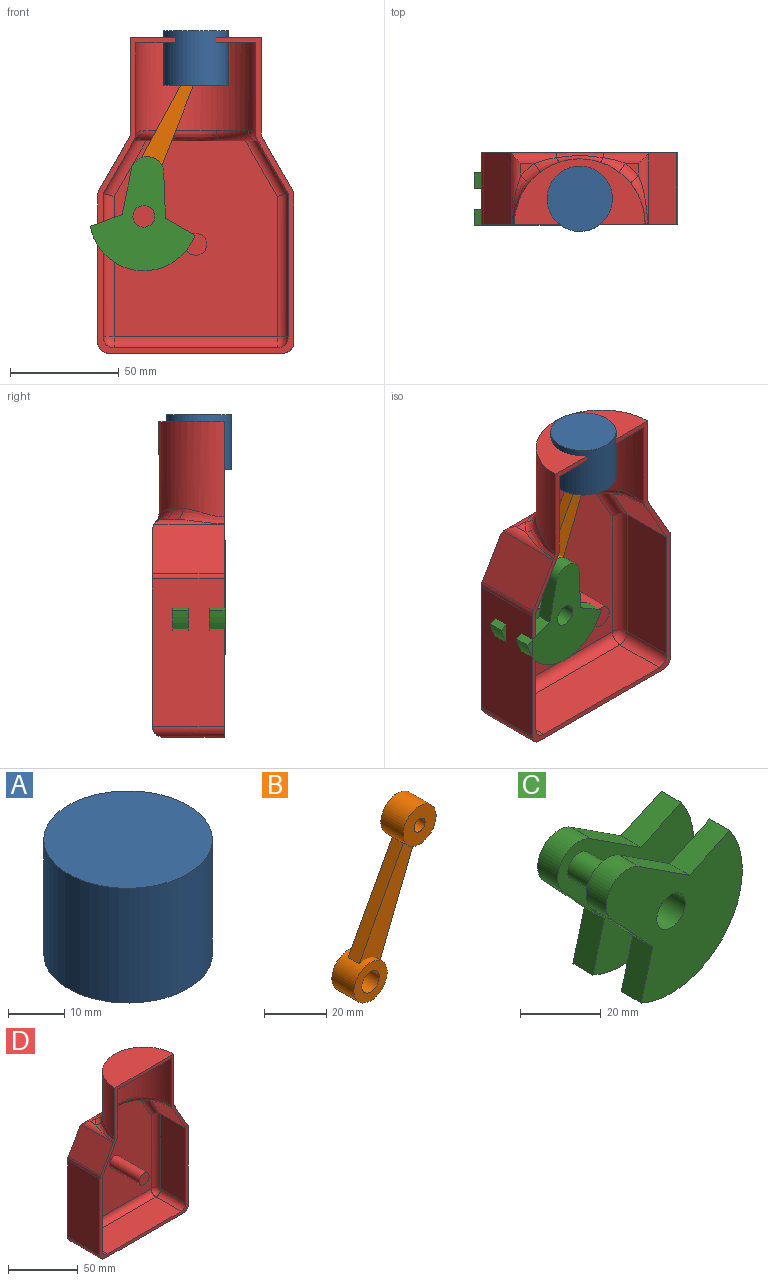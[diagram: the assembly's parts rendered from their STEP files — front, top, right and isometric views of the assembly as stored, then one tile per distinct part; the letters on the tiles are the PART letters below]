
ASSEMBLY  parts=4 mates=3
PART A: 17 faces, bbox 30x30x25 mm
  f0: cylinder r=5mm len=10mm, axis (0,1,0), area 101.5mm2, adj f1,f7,f8,f11
  f1: cylinder r=12mm len=24mm, axis (0,0,1), area 1330.9mm2, adj f0,f2,f3,f6,f7,f8,f9
  f2: plane 21.82x7mm, normal (0,0,-1), area 109.8mm2, adj f1,f7
  f3: plane 30x30mm, normal (0,0,-1), area 254.5mm2, adj f1,f4
  f4: cylinder r=15mm len=30mm, axis (0,0,1), area 2356.2mm2, adj f3,f5
  f5: plane 30x30mm, normal (0,0,1), area 706.9mm2, adj f4
  f6: plane 21.82x7mm, normal (0,0,-1), area 109.8mm2, adj f1,f8
  f7: plane 21.82x12mm, normal (-1,0,0), area 181.8mm2, adj f0,f1,f2,f9,f10,f11,f12
  f8: plane 21.82x12mm, normal (1,0,0), area 181.8mm2, adj f0,f1,f6,f9,f10,f11,f12
  f9: cylinder r=5mm len=10mm, axis (0,1,0), area 101.5mm2, adj f1,f7,f8,f12
  f10: plane 10x10mm, normal (0,0,-1), area 100mm2, adj f7,f8,f11,f12
  f11: plane 13x10mm, normal (0,-1,0), area 99.6mm2, adj f0,f7,f8,f10,f15
  f12: plane 13x10mm, normal (0,1,0), area 99.6mm2, adj f7,f8,f9,f10,f14
  f13: cylinder r=12mm len=5mm, axis (0,0,1), area 19.7mm2, adj f14
  f14: cylinder r=2.5mm len=7mm, axis (0,1,0), area 107.9mm2, adj f12,f13
  f15: cylinder r=2.5mm len=7mm, axis (0,1,0), area 107.9mm2, adj f11,f16
  f16: cylinder r=12mm len=5mm, axis (0,0,1), area 19.7mm2, adj f15
PART B: 12 faces, bbox 37.2x10x65.3 mm
  f0: cylinder r=4mm len=10mm, axis (0,1,0), area 251.3mm2, adj f2,f3
  f1: cylinder r=7.5mm len=15mm, axis (0,1,0), area 416.5mm2, adj f2,f3,f8,f9,f10,f11
  f2: plane 15x15mm, normal (0,-1,0), area 126.4mm2, adj f0,f1
  f3: plane 15x15mm, normal (0,1,0), area 126.4mm2, adj f0,f1
  f4: cylinder r=2.5mm len=10mm, axis (0,1,0), area 157.1mm2, adj f6,f7
  f5: cylinder r=7.5mm len=15mm, axis (0,1,0), area 445.8mm2, adj f6,f7,f8,f9,f10,f11
  f6: plane 15x15mm, normal (0,-1,0), area 157.1mm2, adj f4,f5
  f7: plane 15x15mm, normal (0,1,0), area 157.1mm2, adj f4,f5
  f8: plane 39.37x15.55mm, normal (0.93,0,-0.37), area 211.6mm2, adj f1,f5,f10,f11
  f9: plane 37.48x20.18mm, normal (-0.88,0,0.47), area 212.8mm2, adj f1,f5,f10,f11
  f10: plane 41.03x24.9mm, normal (0,-1,0), area 302.2mm2, adj f1,f5,f8,f9
  f11: plane 41.03x24.9mm, normal (0,1,0), area 302.2mm2, adj f1,f5,f8,f9
PART C: 19 faces, bbox 47.8x24x45.4 mm
  f0: plane 14.12x7mm, normal (-0.42,0,0.91), area 109mm2, adj f1,f6,f7,f10
  f1: plane 17.66x11.48mm, normal (0.55,0,0.84), area 147.5mm2, adj f0,f2,f7,f10
  f2: cylinder r=7.5mm len=12.62mm, axis (0,1,0), area 152.2mm2, adj f1,f3,f7,f10
  f3: plane 15.4x14.38mm, normal (-0.73,0,-0.68), area 147.5mm2, adj f2,f4,f7,f10
  f4: plane 15.05x7mm, normal (-0.97,0,0.26), area 109mm2, adj f3,f6,f7,f10
  f5: cylinder r=5mm len=10mm, axis (0,1,0), area 219.9mm2, adj f7,f10
  f6: cylinder r=25mm len=39.24mm, axis (0,1,0), area 456.5mm2, adj f0,f4,f7,f10
  f7: plane 47.82x45.36mm, normal (0,-1,0), area 1242mm2, adj f0,f1,f2,f3,f4,f5,f6
  f8: cylinder r=4mm len=10mm, axis (0,-1,0), area 251.3mm2, adj f9,f10
  f9: plane 47.82x45.36mm, normal (0,-1,0), area 1191.7mm2, adj f8,f11,f13,f14,f15,f16,f17,f18
  f10: plane 47.82x45.36mm, normal (0,1,0), area 1191.7mm2, adj f0,f1,f2,f3,f4,f5,f6,f8
  f11: cylinder r=5mm len=10mm, axis (0,1,0), area 219.9mm2, adj f9,f12
  f12: plane 47.82x45.36mm, normal (0,1,0), area 1242mm2, adj f11,f13,f14,f15,f16,f17,f18
  f13: cylinder r=25mm len=39.24mm, axis (0,1,0), area 456.5mm2, adj f9,f12,f14,f18
  f14: plane 15.05x7mm, normal (-0.97,0,0.26), area 109mm2, adj f9,f12,f13,f15
  f15: plane 15.4x14.38mm, normal (-0.73,0,-0.68), area 147.5mm2, adj f9,f12,f14,f16
  f16: cylinder r=7.5mm len=12.62mm, axis (0,1,0), area 152.2mm2, adj f9,f12,f15,f17
  f17: plane 17.66x11.48mm, normal (0.55,0,0.84), area 147.5mm2, adj f9,f12,f16,f18
  f18: plane 14.12x7mm, normal (-0.42,0,0.91), area 109mm2, adj f9,f12,f13,f17
PART D: 54 faces, bbox 91.2x35.8x146.2 mm
  f0: plane 6.11x5.87mm, normal (0,0,1), area 16.5mm2, adj f35,f36,f46
  f1: plane 18.55x16.2mm, normal (0,0,-1), area 91.6mm2, adj f19,f20,f21,f31
  f2: cylinder r=30mm len=60mm, axis (0,0,-1), area 3892.7mm2, adj f3,f4,f45,f46,f47,f48,f49,f50
  f3: plane 60x30mm, normal (0,0,1), area 1413.7mm2, adj f2,f4
  f4: plane 145.01x90.01mm, normal (0,-1,0), area 1094.6mm2, adj f2,f3,f6,f7,f8,f9,f10,f12
  f5: plane 6.11x5.87mm, normal (0,0,1), area 16.5mm2, adj f38,f39,f50
  f6: plane 33.05x22.37mm, normal (-0.87,0,0.5), area 849.9mm2, adj f4,f11,f38,f39,f40
  f7: plane 67.68x33mm, normal (-1,0,0), area 2233.4mm2, adj f4,f11,f40,f43
  f8: plane 80x28mm, normal (0,0,-1), area 2240mm2, adj f4,f41,f42,f43
  f9: plane 67.68x33mm, normal (1,0,0), area 2233.4mm2, adj f4,f11,f41,f44
  f10: plane 33.05x22.37mm, normal (0.87,0,0.5), area 849.9mm2, adj f4,f11,f35,f36,f44
  f11: plane 90.42x90mm, normal (0,1,0), area 7850.2mm2, adj f6,f7,f9,f10,f36,f37,f38,f40
  f12: cylinder r=27.5mm len=55mm, axis (0,0,-1), area 3482.1mm2, adj f4,f13,f30,f31,f32,f33,f34
  f13: plane 55x27.5mm, normal (0,0,-1), area 1187.9mm2, adj f4,f12
  f14: plane 18.55x16.2mm, normal (0,0,-1), area 91.6mm2, adj f15,f20,f24,f33
  f15: plane 25.97x24.62mm, normal (0.87,0,-0.5), area 711.1mm2, adj f4,f14,f16,f24,f34
  f16: plane 65.85x25.5mm, normal (1,0,0), area 1679.2mm2, adj f4,f15,f26,f29
  f17: plane 75x25.5mm, normal (0,0,1), area 1912.5mm2, adj f4,f23,f27,f29
  f18: plane 65.85x25.5mm, normal (-1,0,0), area 1679.2mm2, adj f4,f19,f22,f23
  f19: plane 25.97x24.62mm, normal (-0.87,0,-0.5), area 711.1mm2, adj f1,f4,f18,f21,f30
  f20: plane 90.19x75.19mm, normal (0,-1,0), area 6296.3mm2, adj f1,f14,f21,f22,f24,f26,f27,f32
  f21: cylinder r=5mm len=29.15mm, axis (-0.5,0,0.87), area 225.1mm2, adj f1,f19,f20,f22
  f22: cylinder r=5mm len=65.85mm, axis (0,0,1), area 511.9mm2, adj f18,f20,f21,f25
  f23: cylinder r=5mm len=25.5mm, axis (0,-1,0), area 200.3mm2, adj f4,f17,f18,f25
  f24: cylinder r=5mm len=29.15mm, axis (-0.5,0,-0.87), area 225.1mm2, adj f14,f15,f20,f26
  f25: sphere r=5mm, area 25mm2, adj f22,f23,f27
  f26: cylinder r=5mm len=65.85mm, axis (0,0,-1), area 511.9mm2, adj f16,f20,f24,f28
  f27: cylinder r=5mm len=75mm, axis (1,0,0), area 589mm2, adj f17,f20,f25,f28
  f28: sphere r=5mm, area 53.5mm2, adj f26,f27,f29
  f29: cylinder r=5mm len=25.5mm, axis (0,1,0), area 200.3mm2, adj f4,f16,f17,f28
  f30: bspline ~17.75x5.33mm, area 70.1mm2, adj f4,f12,f19,f31
  f31: torus R=32.5mm, axis (0,0,-1), area 165.9mm2, adj f1,f12,f30,f32
  f32: bspline ~23.84x5.32mm, area 131.8mm2, adj f12,f20,f31,f33
  f33: torus R=32.5mm, axis (0,0,-1), area 165.9mm2, adj f12,f14,f32,f34
  f34: bspline ~17.75x5.33mm, area 70.1mm2, adj f4,f12,f15,f33
  f35: cylinder r=5mm len=32.33mm, axis (0,-1,0), area 92.5mm2, adj f0,f4,f10,f36,f45
  f36: cylinder r=5mm len=22.12mm, axis (1,0,0), area 138.6mm2, adj f0,f10,f11,f35,f37,f47
  f37: bspline ~25.2x5.78mm, area 89.9mm2, adj f11,f36,f38,f48
  f38: cylinder r=5mm len=22.12mm, axis (1,0,0), area 138.6mm2, adj f5,f6,f11,f37,f39,f49
  f39: cylinder r=5mm len=32.33mm, axis (0,1,0), area 92.5mm2, adj f4,f5,f6,f38,f51
  f40: cylinder r=5mm len=33mm, axis (0,-1,0), area 86.4mm2, adj f4,f6,f7,f11
  f41: cylinder r=5mm len=33mm, axis (0,1,0), area 239.5mm2, adj f4,f8,f9,f42
  f42: cylinder r=5mm len=90mm, axis (-1,0,0), area 667.6mm2, adj f8,f11,f41,f43
  f43: cylinder r=5mm len=33mm, axis (0,-1,0), area 239.5mm2, adj f4,f7,f8,f42
  f44: cylinder r=5mm len=33mm, axis (0,-1,0), area 86.4mm2, adj f4,f9,f10,f11
  f45: bspline ~24.24x8.76mm, area 107.8mm2, adj f2,f4,f35,f46
  f46: torus R=35mm, axis (0,0,-1), area 60.6mm2, adj f0,f2,f45,f47
  f47: bspline ~15.05x8.61mm, area 64.1mm2, adj f2,f36,f46,f48
  f48: bspline ~23.35x4.66mm, area 88.1mm2, adj f2,f37,f47,f49
  f49: bspline ~15.05x8.61mm, area 64.1mm2, adj f2,f38,f48,f50
  f50: torus R=35mm, axis (0,0,-1), area 60.6mm2, adj f2,f5,f49,f51
  f51: bspline ~24.24x8.76mm, area 107.8mm2, adj f2,f4,f39,f50
  f52: cylinder r=5mm len=30.45mm, axis (0,1,0), area 956.6mm2, adj f20,f53
  f53: plane 10x10mm, normal (0,-1,0), area 78.5mm2, adj f52
PLACE A t=(0,11.67,67.42)mm
PLACE B t=(0,11.67,71.06)mm
PLACE C rot(axis=(0,1,0),54.8deg) t=(-23.87,11.67,62.85)mm
PLACE D at identity fixed
MATE revolute B.f0 <-> C.f2  axis (0,1,0) through (-22.21,11.67,82.78)mm
MATE slider A.f1 <-> D.f13  axis (0,0,1) through (0,11.67,148.09)mm
MATE revolute A.f0 <-> B.f4  axis (0,1,0) through (0,16.67,133.09)mm
